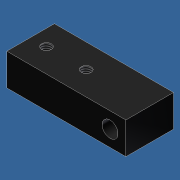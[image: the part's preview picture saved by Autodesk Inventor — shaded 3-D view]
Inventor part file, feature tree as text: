
AUTODESK INVENTOR PART (.ipt)
format: ipt  version: 2012 (Build 160160000, 160)  size: 84,992 bytes
history: native  units: in
note: dims shown in document units (in); Inventor stores cm internally (conversion verified against a paired STEP export)
features: extrude x1, hole x1, pattern_linear x1, sketch x1
ambient origin geometry x8: Origin, YZ Plane, XZ Plane, XY Plane, X Axis, Y Axis, Z Axis, Center Point
bodies: Solid1 (feature_tree)
feature tree (4):
  extrude  "Extrusion1"  Depth=3.75in
  hole  "Hole1"  [1 undecoded]
  pattern_linear  "Rectangular Pattern1"  Spacing1=0.5in  [1 undecoded]
  sketch  "Sketch1"  dims[d0=1.0in d1=3.75in d2=0.5in d3=0.5in d4=0.5in d5=1.5in d6=0.0in d7=0.75in d8=0.5in d9=0.307in d10=0.75in d11=0.375in d12=0.25in d13=0.5635in d14=1.0in d15=0.8108in d16=0.7874in d18=1.25in]
note: 2 required parameter values undecoded (feature->parameter linkage not recoverable at this tier; creation-order binding heuristic only, values carry confidence <= 0.55)
